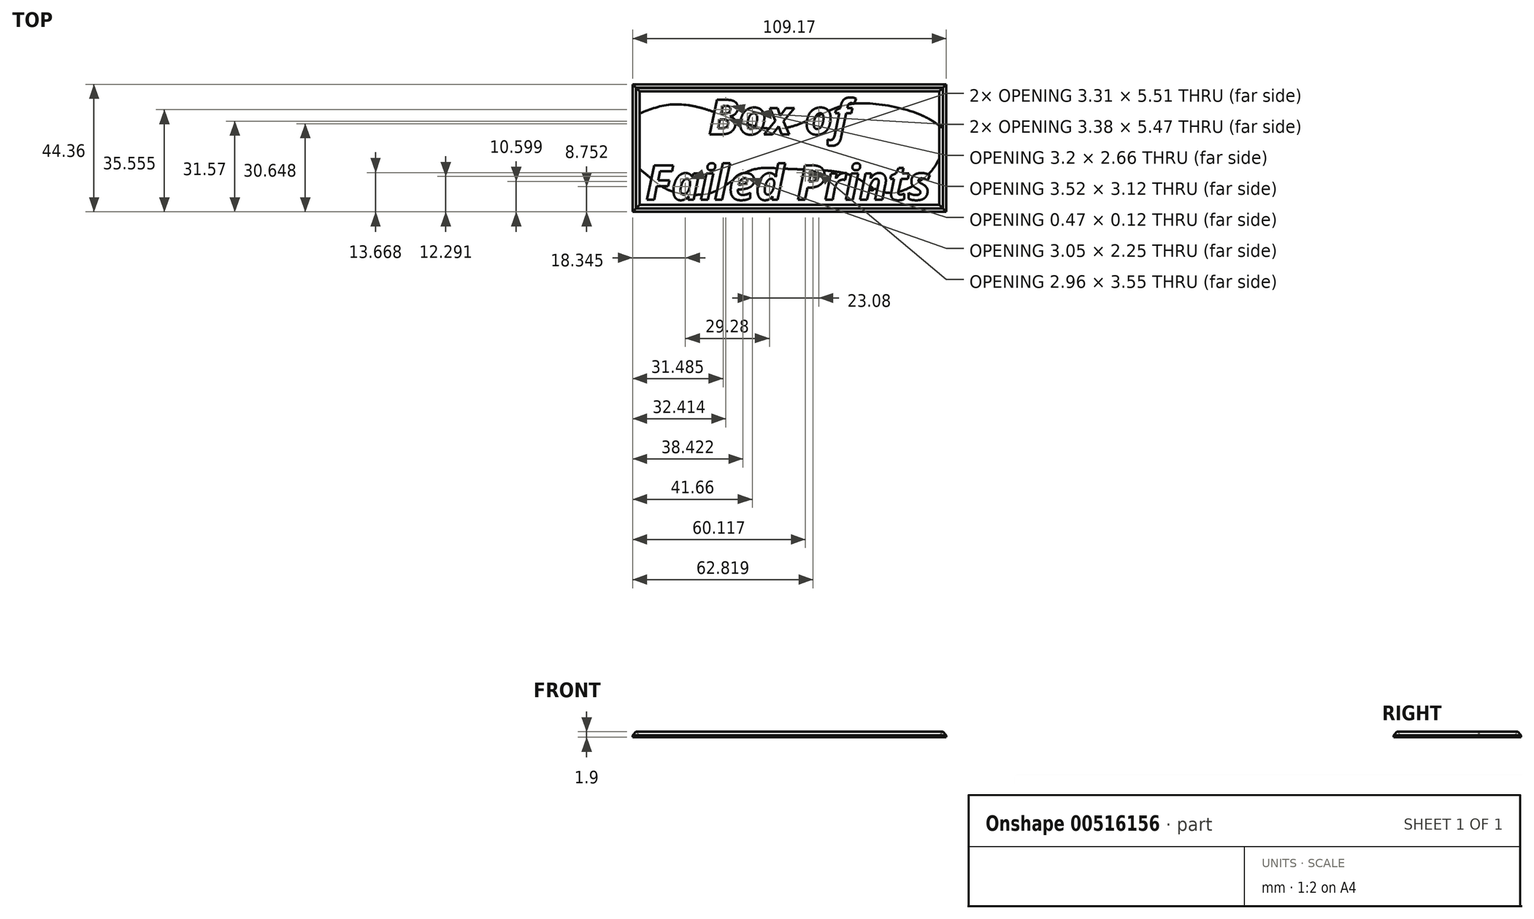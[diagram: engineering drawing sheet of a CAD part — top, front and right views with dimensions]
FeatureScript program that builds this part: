
annotation { "Feature Type Name" : "Feature", "Feature Type Description" : "" }
export const myFeature = defineFeature(function(context is Context, id is Id, definition is map)
    precondition{}
    {
        {
            var Q0;
            Q0=qCreatedBy(makeId("Top.planeOp"),FACE);
            var sketch = newSketch(context, id + "F0", { "sketchPlane" : qUnion([Q0])});
            skText(sketch, "E0", { "text": "     Box of\nFailed Prints", "fontName": "OpenSans-BoldItalic.ttf"});
            skPoint(sketch, "E1", {"position": v(22.9, -6.3) * mm});
            skPoint(sketch, "E2", {"position": v(16.26, 3.29) * mm});
            skPoint(sketch, "E3", {"position": v(-27.04, 4.89) * mm});
            skPoint(sketch, "E4", {"position": v(-27.69, -6.3) * mm});
            skPoint(sketch, "E5", {"position": v(-42.06, -6.3) * mm});
            skPoint(sketch, "E6", {"position": v(38.07, -7.94) * mm});
            skPoint(sketch, "E7", {"position": v(3.67, -16.5) * mm});
            skPoint(sketch, "E8", {"position": v(-5.3, -16.52) * mm});
            skPoint(sketch, "E9", {"position": v(-5.3, 13.1) * mm});
            const initialGuessF0  = {"E0": [-0.0504, 0.00489, 1, 0, 0.01208]};
            skSetInitialGuess(sketch, initialGuessF0);
            skSolve(sketch);
        }
        {
            var Q0;
            Q0=qCreatedBy(makeId("Top.planeOp"),FACE);
            var sketch = newSketch(context, id + "F1", { "sketchPlane" : qUnion([Q0])});
            skLineSegment(sketch, "E10.bottom", {"start": v(-53.75, 21.06) * mm, "end": v(53.02, 21.06) * mm});
            skLineSegment(sketch, "E10.top", {"start": v(-53.75, -20.9) * mm, "end": v(53.02, -20.9) * mm});
            skLineSegment(sketch, "E10.left", {"start": v(-53.75, 21.06) * mm, "end": v(-53.75, -20.9) * mm});
            skLineSegment(sketch, "E10.right", {"start": v(53.02, 21.06) * mm, "end": v(53.02, -20.9) * mm});
            skLineSegment(sketch, "E11.0", {"start": v(-52.55, 19.86) * mm, "end": v(-52.55, 13.08) * mm});
            skLineSegment(sketch, "E11.1", {"start": v(-52.55, 19.86) * mm, "end": v(51.82, 19.86) * mm});
            skLineSegment(sketch, "E11.2", {"start": v(51.82, 19.86) * mm, "end": v(51.82, 8.93) * mm});
            skLineSegment(sketch, "E11.3", {"start": v(-52.55, -19.7) * mm, "end": v(51.82, -19.7) * mm});
            skFitSpline(sketch, "E12", {"points": [v(-52.55, 12.11) * mm, v(-42.33, 15.16) * mm, v(-30.5, 13.9) * mm, v(-17.06, 9.07) * mm, v(-1.82, 7.1) * mm, v(13.59, 13.2) * mm, v(25.42, 15.7) * mm, v(45.49, 11.56) * mm, v(51.82, 7.63) * mm, v(51.82, 7.46) * mm], "startDerivative": vector(90.6, 35.73) * mm, "endDerivative": vector(-3.96, -10.27) * mm});
            skFitSpline(sketch, "E13.0", {"points": [v(-52.88, 12.95) * mm, v(-51.94, 13.32) * mm, v(-50.04, 14.07) * mm, v(-47.12, 15.09) * mm, v(-44.6, 15.73) * mm, v(-42.52, 16.06) * mm, v(-40.4, 16.25) * mm, v(-37.68, 16.2) * mm, v(-34.39, 15.79) * mm, v(-31.07, 15.05) * mm, v(-27.78, 14.03) * mm, v(-24.51, 12.82) * mm, v(-21.23, 11.54) * mm, v(-17.9, 10.29) * mm, v(-14.49, 9.15) * mm, v(-11, 8.25) * mm, v(-8.07, 7.8) * mm, v(-5.72, 7.68) * mm, v(-3.95, 7.72) * mm, v(-2.19, 7.92) * mm, v(-0.42, 8.29) * mm, v(1.36, 8.8) * mm, v(3.74, 9.64) * mm, v(6.7, 10.92) * mm, v(10.13, 12.59) * mm, v(13.4, 14.14) * mm, v(16.47, 15.33) * mm, v(19.03, 16.02) * mm, v(21.17, 16.37) * mm, v(22.85, 16.54) * mm, v(24.62, 16.61) * mm, v(26.53, 16.59) * mm, v(28.55, 16.47) * mm, v(31.37, 16.19) * mm, v(35.04, 15.62) * mm, v(39.45, 14.62) * mm, v(42.95, 13.55) * mm, v(45.52, 12.55) * mm, v(47.3, 11.73) * mm, v(48.62, 11.03) * mm, v(49.57, 10.48) * mm, v(50.2, 10.08) * mm, v(50.78, 9.7) * mm, v(51.29, 9.34) * mm, v(51.72, 9.02) * mm, v(52.02, 8.76) * mm, v(52.22, 8.57) * mm, v(52.35, 8.43) * mm, v(52.48, 8.28) * mm, v(52.6, 8.1) * mm, v(52.72, 7.84) * mm, v(52.76, 7.5) * mm, v(52.7, 7.22) * mm, v(52.67, 7.14) * mm, v(52.66, 7.13) * mm]});
            skFitSpline(sketch, "E14", {"points": [v(-52.55, -7.16) * mm, v(-49.85, -9.38) * mm, v(-43.76, -13.86) * mm, v(-37.3, -15.83) * mm, v(-27.63, -15.47) * mm, v(-19.39, -10.64) * mm, v(-12.04, -7.16) * mm, v(-0.93, -7.16) * mm, v(18.79, -8.66) * mm, v(26.5, -12.43) * mm, v(33.66, -15.47) * mm, v(42.08, -13.32) * mm, v(49.61, -7.16) * mm, v(51.82, -3.29) * mm], "startDerivative": vector(48.53, -39.74) * mm, "endDerivative": vector(29.49, 66.57) * mm});
            skFitSpline(sketch, "E15.0", {"points": [v(-53.19, -7.93) * mm, v(-52.93, -8.14) * mm, v(-52.43, -8.55) * mm, v(-51.61, -9.22) * mm, v(-50.84, -9.86) * mm, v(-50.13, -10.46) * mm, v(-49.35, -11.1) * mm, v(-48.28, -11.97) * mm, v(-46.9, -13.03) * mm, v(-45.43, -14.05) * mm, v(-43.43, -15.23) * mm, v(-41.46, -16) * mm, v(-39.4, -16.51) * mm, v(-38.03, -16.74) * mm, v(-36.88, -16.9) * mm, v(-35.68, -17.04) * mm, v(-34.1, -17.16) * mm, v(-32.13, -17.2) * mm, v(-30.12, -17.05) * mm, v(-28.47, -16.76) * mm, v(-27.17, -16.4) * mm, v(-25.92, -15.94) * mm, v(-24.45, -15.23) * mm, v(-22.8, -14.23) * mm, v(-21.24, -13.17) * mm, v(-19.74, -12.1) * mm, v(-18.3, -11.09) * mm, v(-16.85, -10.18) * mm, v(-15.42, -9.4) * mm, v(-13.98, -8.75) * mm, v(-12.5, -8.26) * mm, v(-11, -7.96) * mm, v(-9.37, -7.82) * mm, v(-7.6, -7.81) * mm, v(-5.67, -7.89) * mm, v(-3.53, -8.02) * mm, v(-1.17, -8.15) * mm, v(1.42, -8.25) * mm, v(4.16, -8.33) * mm, v(7.92, -8.45) * mm, v(11.67, -8.64) * mm, v(15.1, -8.99) * mm, v(17.05, -9.3) * mm, v(18.43, -9.6) * mm, v(19.7, -9.94) * mm, v(21.1, -10.46) * mm, v(22.56, -11.17) * mm, v(23.92, -11.96) * mm, v(25.25, -12.82) * mm, v(26.66, -13.72) * mm, v(28.15, -14.6) * mm, v(29.73, -15.4) * mm, v(31.4, -16.04) * mm, v(32.87, -16.4) * mm, v(34.08, -16.53) * mm, v(35.3, -16.55) * mm, v(36.83, -16.4) * mm, v(38.66, -15.95) * mm, v(40.47, -15.27) * mm, v(42.26, -14.4) * mm, v(44.02, -13.36) * mm, v(45.71, -12.18) * mm, v(47.3, -10.93) * mm, v(48.73, -9.63) * mm, v(49.76, -8.55) * mm, v(50.46, -7.7) * mm, v(51.08, -6.87) * mm, v(51.7, -5.88) * mm, v(52.27, -4.75) * mm, v(52.58, -4.04) * mm, v(52.74, -3.7) * mm]});
            skLineSegment(sketch, "E16.trimOffspring", {"start": v(51.82, 7.63) * mm, "end": v(51.82, -3.29) * mm});
            skLineSegment(sketch, "E17.trimOffspring", {"start": v(51.82, -5.61) * mm, "end": v(51.82, -19.7) * mm});
            skLineSegment(sketch, "E18.trimOffspring", {"start": v(-52.55, 12.11) * mm, "end": v(-52.55, -7.16) * mm});
            skLineSegment(sketch, "E19.trimOffspring", {"start": v(-52.55, -8.45) * mm, "end": v(-52.55, -19.7) * mm});
            skPoint(sketch, "E20.0", {"position": v(-27.04, 4.89) * mm});
            skPoint(sketch, "E20.1", {"position": v(-5.3, 13.1) * mm});
            skPoint(sketch, "E20.2", {"position": v(16.26, 3.29) * mm});
            skPoint(sketch, "E20.3", {"position": v(-5.3, -16.52) * mm});
            skPoint(sketch, "E20.4", {"position": v(-27.69, -6.3) * mm});
            skPoint(sketch, "E20.5", {"position": v(-42.06, -6.3) * mm});
            skPoint(sketch, "E20.6", {"position": v(3.67, -16.5) * mm});
            skPoint(sketch, "E20.7", {"position": v(22.9, -6.3) * mm});
            skPoint(sketch, "E20.8", {"position": v(38.07, -7.94) * mm});
            skFitSpline(sketch, "E21", {"points": [v(-35.55, 15.92) * mm, v(-25.39, 9.77) * mm, v(-23.01, 5.5) * mm, v(-24.33, 2.44) * mm, v(-26.78, 3.1) * mm, v(-27.04, 4.89) * mm], "startDerivative": vector(35.65, -18.2) * mm, "endDerivative": vector(1.74, 14.88) * mm});
            skFitSpline(sketch, "E22", {"points": [v(-35.55, 15.01) * mm, v(-29.48, 12.09) * mm, v(-25.39, 9.28) * mm, v(-23.35, 6.22) * mm, v(-23.45, 3.7) * mm, v(-24.09, 2.78) * mm, v(-24.86, 2.44) * mm, v(-26.1, 2.71) * mm, v(-26.82, 3.4) * mm, v(-27.04, 4.37) * mm, v(-27.04, 4.89) * mm], "startDerivative": vector(34.55, -15.73) * mm, "endDerivative": vector(0.34, 9.11) * mm});
            skFitSpline(sketch, "E23.trimOffspring", {"points": [v(-52.55, 12.11) * mm, v(-42.33, 15.16) * mm, v(-30.5, 13.9) * mm, v(-17.06, 9.07) * mm, v(-1.82, 7.1) * mm, v(13.59, 13.2) * mm, v(25.42, 15.7) * mm, v(45.49, 11.56) * mm, v(51.82, 7.63) * mm, v(51.82, 7.46) * mm], "startDerivative": vector(90.6, 35.73) * mm, "endDerivative": vector(-3.96, -10.27) * mm});
            skFitSpline(sketch, "E24", {"points": [v(-13.88, 9.02) * mm, v(-6.17, 9.6) * mm, v(-1.93, 11.84) * mm, v(-1.44, 14.92) * mm, v(-3.77, 16.71) * mm, v(-5.64, 15.08) * mm, v(-5.3, 13.1) * mm], "startDerivative": vector(33.33, 0.29) * mm, "endDerivative": vector(6.62, -15.63) * mm});
            skFitSpline(sketch, "E25.0", {"points": [v(-13.88, 9.22) * mm, v(-12.5, 9.23) * mm, v(-10.41, 9.25) * mm, v(-7.81, 9.49) * mm, v(-5.99, 9.81) * mm, v(-4.34, 10.33) * mm, v(-2.96, 11.05) * mm, v(-1.97, 11.98) * mm, v(-1.52, 12.94) * mm, v(-1.4, 13.75) * mm, v(-1.46, 14.36) * mm, v(-1.64, 14.95) * mm, v(-1.97, 15.5) * mm, v(-2.4, 15.98) * mm, v(-2.91, 16.33) * mm, v(-3.44, 16.52) * mm, v(-3.95, 16.52) * mm, v(-4.44, 16.32) * mm, v(-4.9, 15.97) * mm, v(-5.25, 15.52) * mm, v(-5.47, 15.03) * mm, v(-5.53, 14.58) * mm, v(-5.47, 14.13) * mm, v(-5.32, 13.66) * mm, v(-5.18, 13.34) * mm, v(-5.11, 13.18) * mm]});
            skFitSpline(sketch, "E26", {"points": [v(11.5, 12.24) * mm, v(18.48, 13.55) * mm, v(26.22, 11.66) * mm, v(28.06, 5.83) * mm, v(25.59, 0.57) * mm, v(17.73, -2.02) * mm, v(15.13, 0) * mm, v(16.26, 3.29) * mm], "startDerivative": vector(41.64, 11.47) * mm, "endDerivative": vector(17.8, 31.18) * mm});
            skFitSpline(sketch, "E27", {"points": [v(9.9, 11.48) * mm, v(16.65, 12.83) * mm, v(20.55, 13.2) * mm, v(25.25, 11.84) * mm, v(27.13, 9.75) * mm, v(27.77, 6.43) * mm, v(27.45, 3.82) * mm, v(26.68, 2.1) * mm, v(25.24, 0.58) * mm, v(21.64, -1.32) * mm, v(18.68, -1.9) * mm, v(17.02, -1.65) * mm, v(15.8, -0.9) * mm, v(15.28, 0.2) * mm, v(15.52, 1.48) * mm, v(16.26, 3.29) * mm], "startDerivative": vector(135.14, 34.44) * mm, "endDerivative": vector(14.14, 33.04) * mm});
            skFitSpline(sketch, "E28", {"points": [v(-48.63, -10.4) * mm, v(-45.26, -11.82) * mm, v(-41.46, -11.12) * mm, v(-40.57, -8.27) * mm, v(-42.06, -6.3) * mm, v(-43.36, -4.79) * mm, v(-43.36, -2.7) * mm], "startDerivative": vector(16.47, -9.34) * mm, "endDerivative": vector(2.3, 15.56) * mm});
            skFitSpline(sketch, "E29", {"points": [v(-45.68, -12.65) * mm, v(-43.36, -12.7) * mm, v(-40.95, -11.57) * mm, v(-39.94, -9.22) * mm, v(-40.64, -7.38) * mm, v(-42.25, -5.9) * mm, v(-43.13, -4.95) * mm, v(-43.37, -4.08) * mm, v(-43.36, -2.7) * mm], "startDerivative": vector(16.29, -2) * mm, "endDerivative": vector(0.67, 13.55) * mm});
            skFitSpline(sketch, "E30", {"points": [v(-22.12, -12.55) * mm, v(-20.64, -10.4) * mm, v(-20.21, -6.84) * mm, v(-22.23, -3.27) * mm, v(-26.98, -2.26) * mm, v(-29.16, -3.7) * mm, v(-29, -5.56) * mm, v(-27.69, -6.3) * mm], "startDerivative": vector(12.43, 14.24) * mm, "endDerivative": vector(14.78, -4.63) * mm});
            skFitSpline(sketch, "E31", {"points": [v(-23.39, -13.4) * mm, v(-21.38, -10.68) * mm, v(-20.58, -8.28) * mm, v(-20.96, -5.77) * mm, v(-22.13, -3.9) * mm, v(-23.4, -2.98) * mm, v(-25.78, -2.41) * mm, v(-27.69, -2.69) * mm, v(-28.82, -3.46) * mm, v(-29.1, -4.42) * mm, v(-29, -5.28) * mm, v(-28.44, -5.9) * mm, v(-27.69, -6.3) * mm], "startDerivative": vector(19.25, 23.31) * mm, "endDerivative": vector(19.53, -7.68) * mm});
            skArc(sketch, "E32", {"start": v(-5.3, -16.52) * mm, "mid": v(-0.45, -13.25) * mm, "end": v(-3.11, -8.04) * mm});
            skPoint(sketch, "E33.3.internal.snap0", {"position": v(-0.45, -13.25) * mm});
            skFitSpline(sketch, "E33", {"points": [v(-5.3, -7.92) * mm, v(-2.64, -8.95) * mm, v(-1.1, -10.64) * mm, v(-0.8, -13.25) * mm, v(-2.05, -15.26) * mm, v(-3.47, -16.08) * mm, v(-5.3, -16.52) * mm], "startDerivative": vector(15.23, -4.5) * mm, "endDerivative": vector(-12.48, -2.45) * mm});
            skArc(sketch, "E34", {"start": v(3.95, -8.33) * mm, "mid": v(-0.22, -12.28) * mm, "end": v(3.67, -16.5) * mm});
            skFitSpline(sketch, "E35", {"points": [v(5.4, -8.37) * mm, v(2.24, -9.29) * mm, v(0.79, -10.56) * mm, v(0, -12.17) * mm, v(0.22, -13.82) * mm, v(1.02, -15.2) * mm, v(2.31, -16.1) * mm, v(3.67, -16.5) * mm], "startDerivative": vector(-16.17, -4.27) * mm, "endDerivative": vector(10.8, -2.51) * mm});
            skFitSpline(sketch, "E36", {"points": [v(13, -8.78) * mm, v(17.88, -10.9) * mm, v(20.1, -12.92) * mm, v(21.11, -14.88) * mm, v(23.58, -16.28) * mm, v(27.13, -15.7) * mm, v(29.54, -13.49) * mm, v(30.3, -10.13) * mm, v(28.27, -7.34) * mm, v(26.05, -6.01) * mm, v(24.72, -5.44) * mm, v(23.01, -5.44) * mm, v(22.9, -6.3) * mm], "startDerivative": vector(45.55, -15.9) * mm, "endDerivative": vector(2.97, -21.58) * mm});
            skFitSpline(sketch, "E37", {"points": [v(17.05, -9.31) * mm, v(19.65, -11.2) * mm, v(21.05, -12.98) * mm, v(21.93, -14.76) * mm, v(24.15, -15.64) * mm, v(27.07, -15.07) * mm, v(29.54, -12.16) * mm, v(30.01, -10.68) * mm, v(29.19, -8.63) * mm, v(26.92, -6.74) * mm, v(24.95, -5.73) * mm, v(23.46, -5.52) * mm, v(23.08, -5.6) * mm, v(22.9, -6.3) * mm], "startDerivative": vector(29.14, -18.97) * mm, "endDerivative": vector(-2.7, -18.66) * mm});
            skFitSpline(sketch, "E38.trimOffspring", {"points": [v(-53.19, -7.93) * mm, v(-52.93, -8.14) * mm, v(-52.43, -8.55) * mm, v(-51.61, -9.22) * mm, v(-50.84, -9.86) * mm, v(-50.13, -10.46) * mm, v(-49.35, -11.1) * mm, v(-48.28, -11.97) * mm, v(-46.9, -13.03) * mm, v(-45.43, -14.05) * mm, v(-43.43, -15.23) * mm, v(-41.46, -16) * mm, v(-39.4, -16.51) * mm, v(-38.03, -16.74) * mm, v(-36.88, -16.9) * mm, v(-35.68, -17.04) * mm, v(-34.1, -17.16) * mm, v(-32.13, -17.2) * mm, v(-30.12, -17.05) * mm, v(-28.47, -16.76) * mm, v(-27.17, -16.4) * mm, v(-25.92, -15.94) * mm, v(-24.45, -15.23) * mm, v(-22.8, -14.23) * mm, v(-21.24, -13.17) * mm, v(-19.74, -12.1) * mm, v(-18.3, -11.09) * mm, v(-16.85, -10.18) * mm, v(-15.42, -9.4) * mm, v(-13.98, -8.75) * mm, v(-12.5, -8.26) * mm, v(-11, -7.96) * mm, v(-9.37, -7.82) * mm, v(-7.6, -7.81) * mm, v(-5.67, -7.89) * mm, v(-3.53, -8.02) * mm, v(-1.17, -8.15) * mm, v(1.42, -8.25) * mm, v(4.16, -8.33) * mm, v(7.92, -8.45) * mm, v(11.67, -8.64) * mm, v(15.1, -8.99) * mm, v(17.05, -9.3) * mm, v(18.43, -9.6) * mm, v(19.7, -9.94) * mm, v(21.1, -10.46) * mm, v(22.56, -11.17) * mm, v(23.92, -11.96) * mm, v(25.25, -12.82) * mm, v(26.66, -13.72) * mm, v(28.15, -14.6) * mm, v(29.73, -15.4) * mm, v(31.4, -16.04) * mm, v(32.87, -16.4) * mm, v(34.08, -16.53) * mm, v(35.3, -16.55) * mm, v(36.83, -16.4) * mm, v(38.66, -15.95) * mm, v(40.47, -15.27) * mm, v(42.26, -14.4) * mm, v(44.02, -13.36) * mm, v(45.71, -12.18) * mm, v(47.3, -10.93) * mm, v(48.73, -9.63) * mm, v(49.76, -8.55) * mm, v(50.46, -7.7) * mm, v(51.08, -6.87) * mm, v(51.7, -5.88) * mm, v(52.27, -4.75) * mm, v(52.58, -4.04) * mm, v(52.74, -3.7) * mm]});
            skLineSegment(sketch, "E39", {"start": v(4.93, -8.5) * mm, "end": v(5.4, -8.37) * mm});
            skFitSpline(sketch, "E40.trimOffspring", {"points": [v(-53.19, -7.93) * mm, v(-52.93, -8.14) * mm, v(-52.43, -8.55) * mm, v(-51.61, -9.22) * mm, v(-50.84, -9.86) * mm, v(-50.13, -10.46) * mm, v(-49.35, -11.1) * mm, v(-48.28, -11.97) * mm, v(-46.9, -13.03) * mm, v(-45.43, -14.05) * mm, v(-43.43, -15.23) * mm, v(-41.46, -16) * mm, v(-39.4, -16.51) * mm, v(-38.03, -16.74) * mm, v(-36.88, -16.9) * mm, v(-35.68, -17.04) * mm, v(-34.1, -17.16) * mm, v(-32.13, -17.2) * mm, v(-30.12, -17.05) * mm, v(-28.47, -16.76) * mm, v(-27.17, -16.4) * mm, v(-25.92, -15.94) * mm, v(-24.45, -15.23) * mm, v(-22.8, -14.23) * mm, v(-21.24, -13.17) * mm, v(-19.74, -12.1) * mm, v(-18.3, -11.09) * mm, v(-16.85, -10.18) * mm, v(-15.42, -9.4) * mm, v(-13.98, -8.75) * mm, v(-12.5, -8.26) * mm, v(-11, -7.96) * mm, v(-9.37, -7.82) * mm, v(-7.6, -7.81) * mm, v(-5.67, -7.89) * mm, v(-3.53, -8.02) * mm, v(-1.17, -8.15) * mm, v(1.42, -8.25) * mm, v(4.16, -8.33) * mm, v(7.92, -8.45) * mm, v(11.67, -8.64) * mm, v(15.1, -8.99) * mm, v(17.05, -9.3) * mm, v(18.43, -9.6) * mm, v(19.7, -9.94) * mm, v(21.1, -10.46) * mm, v(22.56, -11.17) * mm, v(23.92, -11.96) * mm, v(25.25, -12.82) * mm, v(26.66, -13.72) * mm, v(28.15, -14.6) * mm, v(29.73, -15.4) * mm, v(31.4, -16.04) * mm, v(32.87, -16.4) * mm, v(34.08, -16.53) * mm, v(35.3, -16.55) * mm, v(36.83, -16.4) * mm, v(38.66, -15.95) * mm, v(40.47, -15.27) * mm, v(42.26, -14.4) * mm, v(44.02, -13.36) * mm, v(45.71, -12.18) * mm, v(47.3, -10.93) * mm, v(48.73, -9.63) * mm, v(49.76, -8.55) * mm, v(50.46, -7.7) * mm, v(51.08, -6.87) * mm, v(51.7, -5.88) * mm, v(52.27, -4.75) * mm, v(52.58, -4.04) * mm, v(52.74, -3.7) * mm]});
            skFitSpline(sketch, "E41.trimOffspring", {"points": [v(-53.19, -7.93) * mm, v(-52.93, -8.14) * mm, v(-52.43, -8.55) * mm, v(-51.61, -9.22) * mm, v(-50.84, -9.86) * mm, v(-50.13, -10.46) * mm, v(-49.35, -11.1) * mm, v(-48.28, -11.97) * mm, v(-46.9, -13.03) * mm, v(-45.43, -14.05) * mm, v(-43.43, -15.23) * mm, v(-41.46, -16) * mm, v(-39.4, -16.51) * mm, v(-38.03, -16.74) * mm, v(-36.88, -16.9) * mm, v(-35.68, -17.04) * mm, v(-34.1, -17.16) * mm, v(-32.13, -17.2) * mm, v(-30.12, -17.05) * mm, v(-28.47, -16.76) * mm, v(-27.17, -16.4) * mm, v(-25.92, -15.94) * mm, v(-24.45, -15.23) * mm, v(-22.8, -14.23) * mm, v(-21.24, -13.17) * mm, v(-19.74, -12.1) * mm, v(-18.3, -11.09) * mm, v(-16.85, -10.18) * mm, v(-15.42, -9.4) * mm, v(-13.98, -8.75) * mm, v(-12.5, -8.26) * mm, v(-11, -7.96) * mm, v(-9.37, -7.82) * mm, v(-7.6, -7.81) * mm, v(-5.67, -7.89) * mm, v(-3.53, -8.02) * mm, v(-1.17, -8.15) * mm, v(1.42, -8.25) * mm, v(4.16, -8.33) * mm, v(7.92, -8.45) * mm, v(11.67, -8.64) * mm, v(15.1, -8.99) * mm, v(17.05, -9.3) * mm, v(18.43, -9.6) * mm, v(19.7, -9.94) * mm, v(21.1, -10.46) * mm, v(22.56, -11.17) * mm, v(23.92, -11.96) * mm, v(25.25, -12.82) * mm, v(26.66, -13.72) * mm, v(28.15, -14.6) * mm, v(29.73, -15.4) * mm, v(31.4, -16.04) * mm, v(32.87, -16.4) * mm, v(34.08, -16.53) * mm, v(35.3, -16.55) * mm, v(36.83, -16.4) * mm, v(38.66, -15.95) * mm, v(40.47, -15.27) * mm, v(42.26, -14.4) * mm, v(44.02, -13.36) * mm, v(45.71, -12.18) * mm, v(47.3, -10.93) * mm, v(48.73, -9.63) * mm, v(49.76, -8.55) * mm, v(50.46, -7.7) * mm, v(51.08, -6.87) * mm, v(51.7, -5.88) * mm, v(52.27, -4.75) * mm, v(52.58, -4.04) * mm, v(52.74, -3.7) * mm]});
            skLineSegment(sketch, "E42", {"start": v(-15.14, 9.4) * mm, "end": v(-11.13, 9.26) * mm});
            skFitSpline(sketch, "E43.trimOffspring", {"points": [v(-52.88, 12.95) * mm, v(-51.94, 13.32) * mm, v(-50.04, 14.07) * mm, v(-47.12, 15.09) * mm, v(-44.6, 15.73) * mm, v(-42.52, 16.06) * mm, v(-40.4, 16.25) * mm, v(-37.68, 16.2) * mm, v(-34.39, 15.79) * mm, v(-31.07, 15.05) * mm, v(-27.78, 14.03) * mm, v(-24.51, 12.82) * mm, v(-21.23, 11.54) * mm, v(-17.9, 10.29) * mm, v(-14.49, 9.15) * mm, v(-11, 8.25) * mm, v(-8.07, 7.8) * mm, v(-5.72, 7.68) * mm, v(-3.95, 7.72) * mm, v(-2.19, 7.92) * mm, v(-0.42, 8.29) * mm, v(1.36, 8.8) * mm, v(3.74, 9.64) * mm, v(6.7, 10.92) * mm, v(10.13, 12.59) * mm, v(13.4, 14.14) * mm, v(16.47, 15.33) * mm, v(19.03, 16.02) * mm, v(21.17, 16.37) * mm, v(22.85, 16.54) * mm, v(24.62, 16.61) * mm, v(26.53, 16.59) * mm, v(28.55, 16.47) * mm, v(31.37, 16.19) * mm, v(35.04, 15.62) * mm, v(39.45, 14.62) * mm, v(42.95, 13.55) * mm, v(45.52, 12.55) * mm, v(47.3, 11.73) * mm, v(48.62, 11.03) * mm, v(49.57, 10.48) * mm, v(50.2, 10.08) * mm, v(50.78, 9.7) * mm, v(51.29, 9.34) * mm, v(51.72, 9.02) * mm, v(52.02, 8.76) * mm, v(52.22, 8.57) * mm, v(52.35, 8.43) * mm, v(52.48, 8.28) * mm, v(52.6, 8.1) * mm, v(52.72, 7.84) * mm, v(52.76, 7.5) * mm, v(52.7, 7.22) * mm, v(52.67, 7.14) * mm, v(52.66, 7.13) * mm]});
            skLineSegment(sketch, "E44", {"start": v(-5.3, 13.1) * mm, "end": v(-4.97, 12.58) * mm});
            skLineSegment(sketch, "E45", {"start": v(-4.97, 12.58) * mm, "end": v(-5.11, 13.18) * mm});
            skArc(sketch, "E46", {"start": v(48.7, 9.94) * mm, "mid": v(36.85, 4.88) * mm, "end": v(38.07, -7.94) * mm});
            skArc(sketch, "E47", {"start": v(45.49, 11.56) * mm, "mid": v(35.57, 4.17) * mm, "end": v(38.07, -7.94) * mm});
            skFitSpline(sketch, "E48.trimOffspring", {"points": [v(-53.19, -7.93) * mm, v(-52.93, -8.14) * mm, v(-52.43, -8.55) * mm, v(-51.61, -9.22) * mm, v(-50.84, -9.86) * mm, v(-50.13, -10.46) * mm, v(-49.35, -11.1) * mm, v(-48.28, -11.97) * mm, v(-46.9, -13.03) * mm, v(-45.43, -14.05) * mm, v(-43.43, -15.23) * mm, v(-41.46, -16) * mm, v(-39.4, -16.51) * mm, v(-38.03, -16.74) * mm, v(-36.88, -16.9) * mm, v(-35.68, -17.04) * mm, v(-34.1, -17.16) * mm, v(-32.13, -17.2) * mm, v(-30.12, -17.05) * mm, v(-28.47, -16.76) * mm, v(-27.17, -16.4) * mm, v(-25.92, -15.94) * mm, v(-24.45, -15.23) * mm, v(-22.8, -14.23) * mm, v(-21.24, -13.17) * mm, v(-19.74, -12.1) * mm, v(-18.3, -11.09) * mm, v(-16.85, -10.18) * mm, v(-15.42, -9.4) * mm, v(-13.98, -8.75) * mm, v(-12.5, -8.26) * mm, v(-11, -7.96) * mm, v(-9.37, -7.82) * mm, v(-7.6, -7.81) * mm, v(-5.67, -7.89) * mm, v(-3.53, -8.02) * mm, v(-1.17, -8.15) * mm, v(1.42, -8.25) * mm, v(4.16, -8.33) * mm, v(7.92, -8.45) * mm, v(11.67, -8.64) * mm, v(15.1, -8.99) * mm, v(17.05, -9.3) * mm, v(18.43, -9.6) * mm, v(19.7, -9.94) * mm, v(21.1, -10.46) * mm, v(22.56, -11.17) * mm, v(23.92, -11.96) * mm, v(25.25, -12.82) * mm, v(26.66, -13.72) * mm, v(28.15, -14.6) * mm, v(29.73, -15.4) * mm, v(31.4, -16.04) * mm, v(32.87, -16.4) * mm, v(34.08, -16.53) * mm, v(35.3, -16.55) * mm, v(36.83, -16.4) * mm, v(38.66, -15.95) * mm, v(40.47, -15.27) * mm, v(42.26, -14.4) * mm, v(44.02, -13.36) * mm, v(45.71, -12.18) * mm, v(47.3, -10.93) * mm, v(48.73, -9.63) * mm, v(49.76, -8.55) * mm, v(50.46, -7.7) * mm, v(51.08, -6.87) * mm, v(51.7, -5.88) * mm, v(52.27, -4.75) * mm, v(52.58, -4.04) * mm, v(52.74, -3.7) * mm]});
            skFitSpline(sketch, "E49.trimOffspring", {"points": [v(13, -8.78) * mm, v(17.88, -10.9) * mm, v(20.1, -12.92) * mm, v(21.11, -14.88) * mm, v(23.58, -16.28) * mm, v(27.13, -15.7) * mm, v(29.54, -13.49) * mm, v(30.3, -10.13) * mm, v(28.27, -7.34) * mm, v(26.05, -6.01) * mm, v(24.72, -5.44) * mm, v(23.01, -5.44) * mm, v(22.9, -6.3) * mm], "startDerivative": vector(45.55, -15.9) * mm, "endDerivative": vector(2.97, -21.58) * mm});
            skLineSegment(sketch, "E50.0", {"start": v(-54.95, 22.26) * mm, "end": v(54.22, 22.26) * mm});
            skLineSegment(sketch, "E50.1", {"start": v(-54.95, 22.26) * mm, "end": v(-54.95, -22.1) * mm});
            skLineSegment(sketch, "E50.2", {"start": v(-54.95, -22.1) * mm, "end": v(54.22, -22.1) * mm});
            skLineSegment(sketch, "E50.3", {"start": v(54.22, 22.26) * mm, "end": v(54.22, -22.1) * mm});
            skSolve(sketch);
        }
        {
            var Q0;
            Q0=makeQuery(id+"F1.imprint","IMPRINT",FACE,{"disambiguationData":[TD([[makeQuery(id+"F1.imprint","IMPRINT",EDGE,{"derivedFrom":sQuery(id+"F1.wireOp",EDGE,"E10.bottom")}),1.0]])]});
            var Q1;
            Q1=makeQuery(id+"F1.imprint","IMPRINT",FACE,{"disambiguationData":[TD([[makeQuery(id+"F1.imprint","IMPRINT",EDGE,{"derivedFrom":sQuery(id+"F1.wireOp",EDGE,"E10.bottom")}),-1.0]])]});
            extrude(context, id + "F2", {"entities" : qUnion([Q0, Q1]), "depth" : .4 * mm, "offsetDistance" : 25 * mm});
        }
        {
            var Q0;
            Q0 = qSketchRegion(id + "F0", true);
            extrude(context, id + "F3", {"entities" : qUnion([Q0]), "depth" : .8 * mm, "offsetDistance" : 25 * mm});
        }
        {
            var Q0;
            Q0=makeQuery(id+"F2.opExtrude","CAP_FACE",FACE,{"disambiguationData":[OSD([sQuery(id+"F1.wireOp",EDGE,"E11.0"),sQuery(id+"F1.wireOp",EDGE,"E11.1"),sQuery(id+"F1.wireOp",EDGE,"E11.2"),sQuery(id+"F1.wireOp",EDGE,"E11.3"),sQuery(id+"F1.wireOp",EDGE,"E12"),sQuery(id+"F1.wireOp",EDGE,"E13.0"),sQuery(id+"F1.wireOp",EDGE,"E14"),sQuery(id+"F1.wireOp",EDGE,"E15.0"),sQuery(id+"F1.wireOp",EDGE,"E16.trimOffspring"),sQuery(id+"F1.wireOp",EDGE,"E17.trimOffspring"),sQuery(id+"F1.wireOp",EDGE,"E18.trimOffspring"),sQuery(id+"F1.wireOp",EDGE,"E19.trimOffspring"),sQuery(id+"F1.wireOp",EDGE,"E21"),sQuery(id+"F1.wireOp",EDGE,"E22"),sQuery(id+"F1.wireOp",EDGE,"E23.trimOffspring"),sQuery(id+"F1.wireOp",EDGE,"E24"),sQuery(id+"F1.wireOp",EDGE,"E25.0"),sQuery(id+"F1.wireOp",EDGE,"E26"),sQuery(id+"F1.wireOp",EDGE,"E27"),sQuery(id+"F1.wireOp",EDGE,"E23.trimOffspring"),sQuery(id+"F1.wireOp",EDGE,"E28"),sQuery(id+"F1.wireOp",EDGE,"E29"),sQuery(id+"F1.wireOp",EDGE,"E14"),sQuery(id+"F1.wireOp",EDGE,"E30"),sQuery(id+"F1.wireOp",EDGE,"E31"),sQuery(id+"F1.wireOp",EDGE,"E32"),sQuery(id+"F1.wireOp",EDGE,"E33"),sQuery(id+"F1.wireOp",EDGE,"E34"),sQuery(id+"F1.wireOp",EDGE,"E35"),sQuery(id+"F1.wireOp",EDGE,"E36"),sQuery(id+"F1.wireOp",EDGE,"E37"),sQuery(id+"F1.wireOp",EDGE,"E38.trimOffspring"),sQuery(id+"F1.wireOp",EDGE,"E39"),sQuery(id+"F1.wireOp",EDGE,"E40.trimOffspring"),sQuery(id+"F1.wireOp",EDGE,"E41.trimOffspring"),sQuery(id+"F1.wireOp",EDGE,"E14"),sQuery(id+"F1.wireOp",EDGE,"E42"),sQuery(id+"F1.wireOp",EDGE,"E43.trimOffspring"),sQuery(id+"F1.wireOp",EDGE,"E44"),sQuery(id+"F1.wireOp",EDGE,"E45"),sQuery(id+"F1.wireOp",EDGE,"E46"),sQuery(id+"F1.wireOp",EDGE,"E47"),sQuery(id+"F1.wireOp",EDGE,"E23.trimOffspring"),sQuery(id+"F1.wireOp",EDGE,"E37"),sQuery(id+"F1.wireOp",EDGE,"E48.trimOffspring"),sQuery(id+"F1.wireOp",EDGE,"E49.trimOffspring"),sQuery(id+"F1.wireOp",EDGE,"E14"),sQuery(id+"F1.wireOp",EDGE,"E50.0"),sQuery(id+"F1.wireOp",EDGE,"E50.1"),sQuery(id+"F1.wireOp",EDGE,"E50.2"),sQuery(id+"F1.wireOp",EDGE,"E50.3")])],"isStart":false});
            var sketch = newSketch(context, id + "F4", { "sketchPlane" : qUnion([Q0])});
            skLineSegment(sketch, "E51", {"start": v(-52.55, 19.86) * mm, "end": v(-54.95, 22.26) * mm});
            skLineSegment(sketch, "E52", {"start": v(-52.55, -19.7) * mm, "end": v(-54.95, -22.1) * mm});
            skLineSegment(sketch, "E53", {"start": v(51.82, -19.7) * mm, "end": v(54.22, -22.1) * mm});
            skLineSegment(sketch, "E54", {"start": v(54.22, 22.26) * mm, "end": v(51.82, 19.86) * mm});
            skLineSegment(sketch, "E55.0", {"start": v(-53.75, 21.06) * mm, "end": v(-53.75, -20.9) * mm});
            skLineSegment(sketch, "E55.1", {"start": v(-53.75, 21.06) * mm, "end": v(53.02, 21.06) * mm});
            skLineSegment(sketch, "E55.2", {"start": v(-53.75, -20.9) * mm, "end": v(53.02, -20.9) * mm});
            skLineSegment(sketch, "E55.3", {"start": v(53.02, 21.06) * mm, "end": v(53.02, -20.9) * mm});
            skLineSegment(sketch, "E56.0", {"start": v(-54.95, 22.26) * mm, "end": v(54.22, 22.26) * mm});
            skLineSegment(sketch, "E56.1", {"start": v(-54.95, 22.26) * mm, "end": v(-54.95, -22.1) * mm});
            skLineSegment(sketch, "E56.2", {"start": v(-54.95, -22.1) * mm, "end": v(54.22, -22.1) * mm});
            skLineSegment(sketch, "E56.3", {"start": v(54.22, 22.26) * mm, "end": v(54.22, -22.1) * mm});
            skLineSegment(sketch, "E56.4", {"start": v(-52.55, 19.86) * mm, "end": v(51.82, 19.86) * mm});
            skLineSegment(sketch, "E56.5", {"start": v(-52.55, -19.7) * mm, "end": v(51.82, -19.7) * mm});
            skLineSegment(sketch, "E56.6", {"start": v(-52.55, 12.11) * mm, "end": v(-52.55, -7.16) * mm});
            skLineSegment(sketch, "E56.7", {"start": v(-52.55, 19.86) * mm, "end": v(-52.55, 13.08) * mm});
            skLineSegment(sketch, "E56.8", {"start": v(-52.55, -8.45) * mm, "end": v(-52.55, -19.7) * mm});
            skLineSegment(sketch, "E56.9", {"start": v(51.82, -5.61) * mm, "end": v(51.82, -19.7) * mm});
            skLineSegment(sketch, "E56.10", {"start": v(51.82, 7.63) * mm, "end": v(51.82, -3.29) * mm});
            skLineSegment(sketch, "E56.11", {"start": v(51.82, 19.86) * mm, "end": v(51.82, 8.93) * mm});
            skLineSegment(sketch, "E57", {"start": v(-52.55, 13.08) * mm, "end": v(-52.55, 12.11) * mm});
            skLineSegment(sketch, "E58", {"start": v(-52.55, -7.16) * mm, "end": v(-52.55, -8.45) * mm});
            skLineSegment(sketch, "E59", {"start": v(51.82, 8.93) * mm, "end": v(51.82, 7.63) * mm});
            skLineSegment(sketch, "E60", {"start": v(51.82, -3.29) * mm, "end": v(51.82, -5.61) * mm});
            skSolve(sketch);
        }
        {
            var Q0;
            {var subQ2=sQuery(id+"F4.wireOp",EDGE,"E55.0");Q0=makeQuery(id+"F4.imprint","IMPRINT",FACE,{"disambiguationData":[TD([[makeQuery(id+"F4.imprint","IMPRINT",EDGE,{"derivedFrom":subQ2}),-1.0]])]});}
            var Q1;
            {var subQ0=sQuery(id+"F4.wireOp",EDGE,"E55.0");Q1=makeQuery(id+"F4.imprint","IMPRINT",FACE,{"disambiguationData":[TD([[makeQuery(id+"F4.imprint","IMPRINT",EDGE,{"derivedFrom":subQ0}),1.0]])]});}
            var Q2;
            {var subQ2=sQuery(id+"F4.wireOp",EDGE,"E55.1");Q2=makeQuery(id+"F4.imprint","IMPRINT",FACE,{"disambiguationData":[TD([[makeQuery(id+"F4.imprint","IMPRINT",EDGE,{"derivedFrom":subQ2}),-1.0]])]});}
            var Q3;
            {var subQ2=sQuery(id+"F4.wireOp",EDGE,"E55.1");Q3=makeQuery(id+"F4.imprint","IMPRINT",FACE,{"disambiguationData":[TD([[makeQuery(id+"F4.imprint","IMPRINT",EDGE,{"derivedFrom":subQ2}),1.0]])]});}
            var Q4;
            {var subQ1=sQuery(id+"F4.wireOp",EDGE,"E55.3");Q4=makeQuery(id+"F4.imprint","IMPRINT",FACE,{"disambiguationData":[TD([[makeQuery(id+"F4.imprint","IMPRINT",EDGE,{"derivedFrom":subQ1}),-1.0]])]});}
            var Q5;
            {var subQ2=sQuery(id+"F4.wireOp",EDGE,"E55.3");Q5=makeQuery(id+"F4.imprint","IMPRINT",FACE,{"disambiguationData":[TD([[makeQuery(id+"F4.imprint","IMPRINT",EDGE,{"derivedFrom":subQ2}),1.0]])]});}
            var Q6;
            {var subQ2=sQuery(id+"F4.wireOp",EDGE,"E55.2");Q6=makeQuery(id+"F4.imprint","IMPRINT",FACE,{"disambiguationData":[TD([[makeQuery(id+"F4.imprint","IMPRINT",EDGE,{"derivedFrom":subQ2}),1.0]])]});}
            var Q7;
            {var subQ2=sQuery(id+"F4.wireOp",EDGE,"E55.2");Q7=makeQuery(id+"F4.imprint","IMPRINT",FACE,{"disambiguationData":[TD([[makeQuery(id+"F4.imprint","IMPRINT",EDGE,{"derivedFrom":subQ2}),-1.0]])]});}
            extrude(context, id + "F5", {"entities" : qUnion([Q0, Q1, Q2, Q3, Q4, Q5, Q6, Q7]), "operationType" : NewBodyOperationType.ADD, "depth" : 1.5 * mm, "offsetDistance" : 25 * mm});
        }
        {
            var Q0;
            Q0=makeQuery(id+"F5.opExtrude","CAP_EDGE",EDGE,{"disambiguationData":[OSD([sQuery(id+"F4.wireOp",EDGE,"E56.1")])],"isStart":false});
            var Q1;
            Q1=makeQuery(id+"F5.opExtrude","CAP_EDGE",EDGE,{"disambiguationData":[OSD([sQuery(id+"F4.wireOp",EDGE,"E56.6"),sQuery(id+"F4.wireOp",EDGE,"E56.7"),sQuery(id+"F4.wireOp",EDGE,"E56.8"),sQuery(id+"F4.wireOp",EDGE,"E57"),sQuery(id+"F4.wireOp",EDGE,"E58")])],"isStart":false});
            var Q2;
            Q2=makeQuery(id+"F5.opExtrude","CAP_EDGE",EDGE,{"disambiguationData":[OSD([sQuery(id+"F4.wireOp",EDGE,"E56.4")])],"isStart":false});
            var Q3;
            Q3=makeQuery(id+"F5.opExtrude","CAP_EDGE",EDGE,{"disambiguationData":[OSD([sQuery(id+"F4.wireOp",EDGE,"E56.0")])],"isStart":false});
            var Q4;
            Q4=makeQuery(id+"F5.opExtrude","CAP_EDGE",EDGE,{"disambiguationData":[OSD([sQuery(id+"F4.wireOp",EDGE,"E56.2")])],"isStart":false});
            var Q5;
            Q5=makeQuery(id+"F5.opExtrude","CAP_EDGE",EDGE,{"disambiguationData":[OSD([sQuery(id+"F4.wireOp",EDGE,"E56.5")])],"isStart":false});
            var Q6;
            Q6=makeQuery(id+"F5.opExtrude","CAP_EDGE",EDGE,{"disambiguationData":[OSD([sQuery(id+"F4.wireOp",EDGE,"E56.3")])],"isStart":false});
            var Q7;
            Q7=makeQuery(id+"F5.opExtrude","CAP_FACE",FACE,{"disambiguationData":[OSD([sQuery(id+"F1.wireOp",EDGE,"E23.trimOffspring"),sQuery(id+"F4.wireOp",EDGE,"E56.0"),sQuery(id+"F4.wireOp",EDGE,"E56.1"),sQuery(id+"F4.wireOp",EDGE,"E56.2"),sQuery(id+"F4.wireOp",EDGE,"E56.3"),sQuery(id+"F4.wireOp",EDGE,"E56.4"),sQuery(id+"F4.wireOp",EDGE,"E56.5"),sQuery(id+"F4.wireOp",EDGE,"E56.6"),sQuery(id+"F4.wireOp",EDGE,"E56.7"),sQuery(id+"F4.wireOp",EDGE,"E56.8"),sQuery(id+"F4.wireOp",EDGE,"E56.9"),sQuery(id+"F4.wireOp",EDGE,"E56.10"),sQuery(id+"F4.wireOp",EDGE,"E56.11"),sQuery(id+"F4.wireOp",EDGE,"E57"),sQuery(id+"F4.wireOp",EDGE,"E58"),sQuery(id+"F4.wireOp",EDGE,"E59"),sQuery(id+"F4.wireOp",EDGE,"E60")])],"isStart":false});
            chamfer(context, id + "F6", {"entities" : qUnion([Q0, Q1, Q2, Q3, Q4, Q5, Q6, Q7]), "width" : 1.18 * mm, "tangentPropagation" : true});
        }
    });
